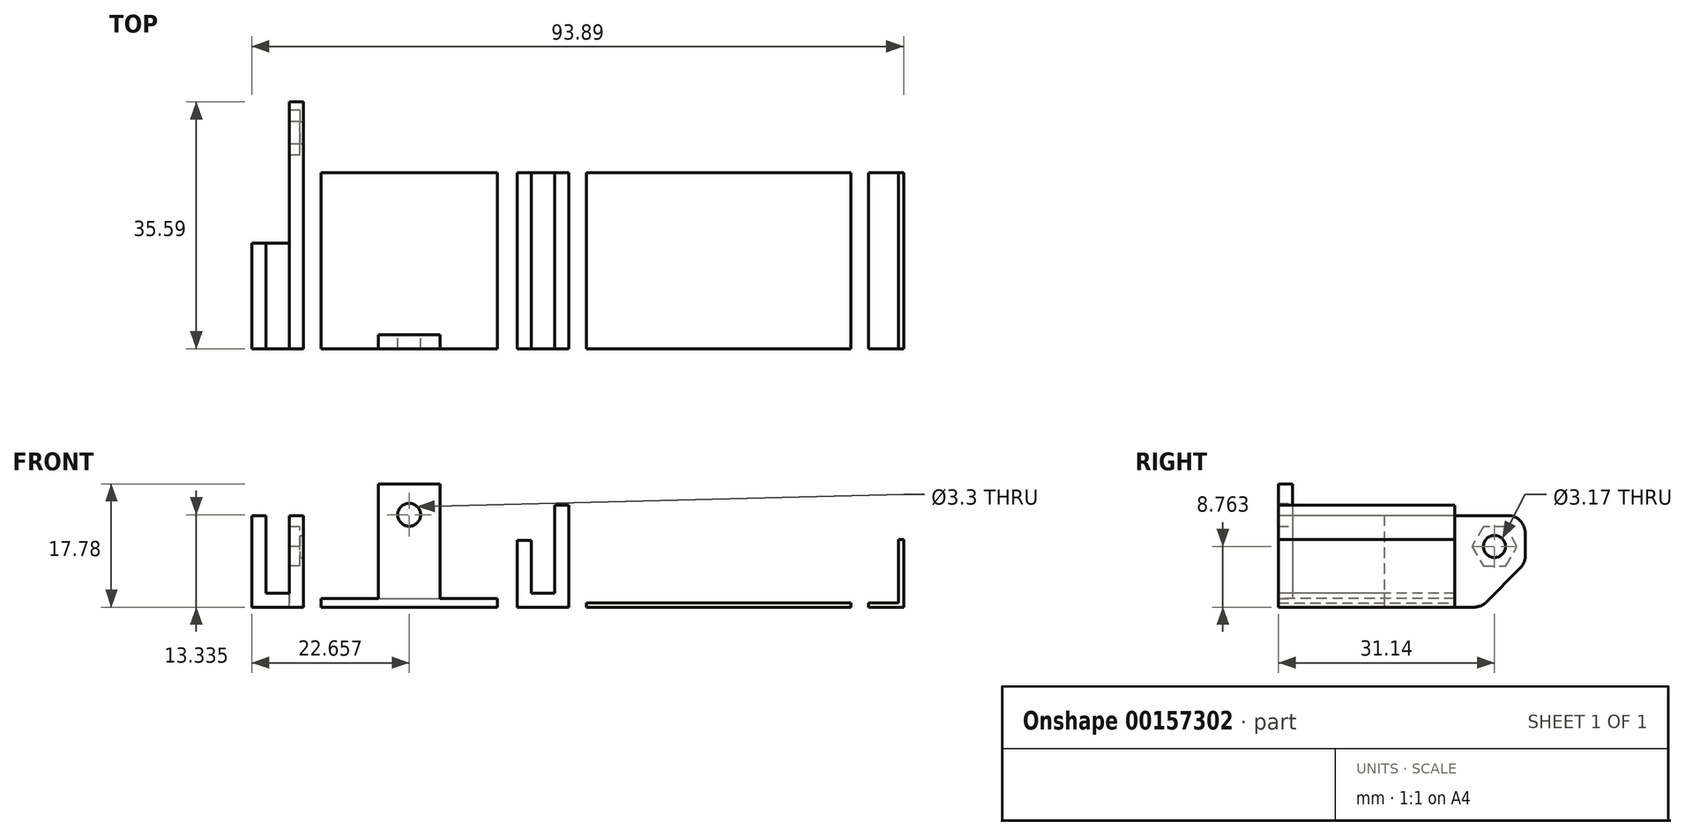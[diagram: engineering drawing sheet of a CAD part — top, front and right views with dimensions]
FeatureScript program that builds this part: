
annotation { "Feature Type Name" : "Feature", "Feature Type Description" : "" }
export const myFeature = defineFeature(function(context is Context, id is Id, definition is map)
    precondition{}
    {
        {
            var Q0;
            Q0=qCreatedBy(makeId("Top.planeOp"),FACE);
            var sketch = newSketch(context, id + "F0", { "sketchPlane" : qUnion([Q0])});
            skLineSegment(sketch, "E0.bottom", {"start": v(2.54, 17.78) * mm, "end": v(9.96, 17.78) * mm});
            skLineSegment(sketch, "E0.top", {"start": v(2.54, 2.54) * mm, "end": v(9.96, 2.54) * mm});
            skLineSegment(sketch, "E0.left", {"start": v(2.54, 17.78) * mm, "end": v(2.54, 2.54) * mm});
            skLineSegment(sketch, "E0.right", {"start": v(9.96, 17.78) * mm, "end": v(9.96, 2.54) * mm});
            skSolve(sketch);
        }
        {
            var Q0;
            Q0 = qSketchRegion(id + "F0", true);
            extrude(context, id + "F1", {"entities" : qUnion([Q0]), "depth" : 2.03 * mm});
        }
        {
            var Q0;
            Q0=makeQuery(id+"F1.opExtrude","CAP_FACE",FACE,{"disambiguationData":[OSD([sQuery(id+"F0.wireOp",EDGE,"E0.bottom"),sQuery(id+"F0.wireOp",EDGE,"E0.top"),sQuery(id+"F0.wireOp",EDGE,"E0.left"),sQuery(id+"F0.wireOp",EDGE,"E0.right")])],"isStart":false});
            var sketch = newSketch(context, id + "F2", { "sketchPlane" : qUnion([Q0])});
            skLineSegment(sketch, "E1.bottom", {"start": v(2.54, 17.78) * mm, "end": v(4.57, 17.78) * mm});
            skLineSegment(sketch, "E1.top", {"start": v(2.54, 2.54) * mm, "end": v(4.57, 2.54) * mm});
            skLineSegment(sketch, "E1.left", {"start": v(2.54, 17.78) * mm, "end": v(2.54, 2.54) * mm});
            skLineSegment(sketch, "E1.right", {"start": v(4.57, 17.78) * mm, "end": v(4.57, 2.54) * mm});
            skLineSegment(sketch, "E2.bottom", {"start": v(9.96, 17.78) * mm, "end": v(7.92, 17.78) * mm});
            skLineSegment(sketch, "E2.top", {"start": v(9.96, 2.54) * mm, "end": v(7.92, 2.54) * mm});
            skLineSegment(sketch, "E2.left", {"start": v(9.96, 17.78) * mm, "end": v(9.96, 2.54) * mm});
            skLineSegment(sketch, "E2.right", {"start": v(7.92, 17.78) * mm, "end": v(7.92, 2.54) * mm});
            skSolve(sketch);
        }
        {
            var Q0;
            Q0 = qSketchRegion(id + "F2", true);
            extrude(context, id + "F3", {"entities" : qUnion([Q0]), "operationType" : NewBodyOperationType.ADD, "depth" : 11.18 * mm});
        }
        {
            var Q0;
            Q0=makeQuery(id+"F3.boolean.opBoolean","MERGE",FACE,{"derivedFrom":[makeQuery(id+"F1.opExtrude","SWEPT_FACE",FACE,{"disambiguationData":[OSD([sQuery(id+"F0.wireOp",EDGE,"E0.right")])]}),makeQuery(id+"F3.opExtrude","SWEPT_FACE",FACE,{"disambiguationData":[OSD([sQuery(id+"F2.wireOp",EDGE,"E2.left")])]})]});
            var sketch = newSketch(context, id + "F4", { "sketchPlane" : qUnion([Q0])});
            skLineSegment(sketch, "E3.bottom", {"start": v(17.78, 0) * mm, "end": v(30.72, 0) * mm});
            skLineSegment(sketch, "E3.top", {"start": v(17.78, 13.2) * mm, "end": v(35.59, 13.2) * mm});
            skLineSegment(sketch, "E3.left", {"start": v(17.78, 0) * mm, "end": v(17.78, 13.2) * mm});
            skLineSegment(sketch, "E3.right", {"start": v(38.13, 7.4) * mm, "end": v(38.13, 10.67) * mm});
            skCircle(sketch, "E4", {"center": v(33.68, 8.76) * mm, "radius": 1.59 * mm});
            skLineSegment(sketch, "E5", {"start": v(32.52, 0.74) * mm, "end": v(37.38, 5.6) * mm});
            skPoint(sketch, "E6.visualSharp", {"position": v(31.78, 0) * mm});
            skArc(sketch, "E6.filletArc", {"start": v(30.72, 0) * mm, "mid": v(31.7, 0.2) * mm, "end": v(32.52, 0.74) * mm});
            skPoint(sketch, "E7.visualSharp", {"position": v(38.13, 6.35) * mm});
            skArc(sketch, "E7.filletArc", {"start": v(37.38, 5.6) * mm, "mid": v(37.93, 6.43) * mm, "end": v(38.13, 7.4) * mm});
            skPoint(sketch, "E8.visualSharp", {"position": v(38.13, 13.2) * mm});
            skArc(sketch, "E8.filletArc", {"start": v(38.13, 10.67) * mm, "mid": v(37.38, 12.46) * mm, "end": v(35.59, 13.2) * mm});
            skSolve(sketch);
        }
        {
            var Q0;
            Q0 = qSketchRegion(id + "F4", true);
            extrude(context, id + "F5", {"entities" : qUnion([Q0]), "operationType" : NewBodyOperationType.ADD, "oppositeDirection" : true, "depth" : 2.03 * mm});
        }
        {
            var Q0;
            Q0=makeQuery(id+"F5.opExtrude","CAP_FACE",FACE,{"disambiguationData":[OSD([sQuery(id+"F4.wireOp",EDGE,"E3.bottom"),sQuery(id+"F4.wireOp",EDGE,"E3.top"),sQuery(id+"F4.wireOp",EDGE,"E3.left"),sQuery(id+"F4.wireOp",EDGE,"E3.right")])],"isStart":false});
            var sketch = newSketch(context, id + "F6", { "sketchPlane" : qUnion([Q0])});
            skCircle(sketch, "E9.cCircle", {"center": v(-33.68, 8.76) * mm, "radius": 2.82 * mm, "construction": true});
            skLineSegment(sketch, "E9.0", {"start": v(-36.94, 8.76) * mm, "end": v(-35.3, 11.58) * mm});
            skLineSegment(sketch, "E9.1", {"start": v(-35.3, 11.58) * mm, "end": v(-32.05, 11.58) * mm});
            skLineSegment(sketch, "E9.2", {"start": v(-32.05, 11.58) * mm, "end": v(-30.42, 8.76) * mm});
            skLineSegment(sketch, "E9.3", {"start": v(-30.42, 8.76) * mm, "end": v(-32.05, 5.94) * mm});
            skLineSegment(sketch, "E9.4", {"start": v(-32.05, 5.94) * mm, "end": v(-35.3, 5.94) * mm});
            skLineSegment(sketch, "E9.5", {"start": v(-35.3, 5.94) * mm, "end": v(-36.94, 8.76) * mm});
            skPoint(sketch, "E9.0.midPoint", {"position": v(-36.12, 10.17) * mm});
            skSolve(sketch);
        }
        {
            var Q0;
            Q0 = qSketchRegion(id + "F6", true);
            extrude(context, id + "F7", {"entities" : qUnion([Q0]), "operationType" : NewBodyOperationType.REMOVE, "oppositeDirection" : true, "depth" : 1.52 * mm});
        }
        {
            var Q0;
            Q0=qCreatedBy(makeId("Top.planeOp"),FACE);
            var sketch = newSketch(context, id + "F8", { "sketchPlane" : qUnion([Q0])});
            skLineSegment(sketch, "E10.bottom", {"start": v(12.5, 27.94) * mm, "end": v(37.9, 27.94) * mm});
            skLineSegment(sketch, "E10.top", {"start": v(12.5, 2.54) * mm, "end": v(37.9, 2.54) * mm});
            skLineSegment(sketch, "E10.left", {"start": v(12.5, 27.94) * mm, "end": v(12.5, 2.54) * mm});
            skLineSegment(sketch, "E10.right", {"start": v(37.9, 27.94) * mm, "end": v(37.9, 2.54) * mm});
            skSolve(sketch);
        }
        {
            var Q0;
            Q0 = qSketchRegion(id + "F8", true);
            extrude(context, id + "F9", {"entities" : qUnion([Q0]), "depth" : 1.27 * mm});
        }
        {
            var Q0;
            Q0=makeQuery(id+"F9.opExtrude","CAP_FACE",FACE,{"disambiguationData":[OSD([sQuery(id+"F8.wireOp",EDGE,"E10.bottom"),sQuery(id+"F8.wireOp",EDGE,"E10.top"),sQuery(id+"F8.wireOp",EDGE,"E10.left"),sQuery(id+"F8.wireOp",EDGE,"E10.right")])],"isStart":false});
            var sketch = newSketch(context, id + "F10", { "sketchPlane" : qUnion([Q0])});
            skLineSegment(sketch, "E11.bottom", {"start": v(20.75, 2.54) * mm, "end": v(29.64, 2.54) * mm});
            skLineSegment(sketch, "E11.top", {"start": v(20.75, 4.57) * mm, "end": v(29.64, 4.57) * mm});
            skLineSegment(sketch, "E11.left", {"start": v(20.75, 2.54) * mm, "end": v(20.75, 4.57) * mm});
            skLineSegment(sketch, "E11.right", {"start": v(29.64, 2.54) * mm, "end": v(29.64, 4.57) * mm});
            skSolve(sketch);
        }
        {
            var Q0;
            Q0 = qSketchRegion(id + "F10", true);
            extrude(context, id + "F11", {"entities" : qUnion([Q0]), "operationType" : NewBodyOperationType.ADD, "depth" : 16.5 * mm});
        }
        {
            var Q0;
            Q0=makeQuery(id+"F11.opExtrude","SWEPT_FACE",FACE,{"disambiguationData":[OSD([sQuery(id+"F10.wireOp",EDGE,"E11.top")])]});
            var sketch = newSketch(context, id + "F12", { "sketchPlane" : qUnion([Q0])});
            skCircle(sketch, "E12", {"center": v(-25.2, 13.34) * mm, "radius": 1.65 * mm});
            skSolve(sketch);
        }
        {
            var Q0;
            Q0 = qSketchRegion(id + "F12", true);
            extrude(context, id + "F13", {"entities" : qUnion([Q0]), "operationType" : NewBodyOperationType.REMOVE, "endBound" : BoundingType.UP_TO_NEXT, "oppositeDirection" : true, "depth" : 25.4 * mm});
        }
        {
            var Q0;
            Q0=qCreatedBy(makeId("Top.planeOp"),FACE);
            var sketch = newSketch(context, id + "F14", { "sketchPlane" : qUnion([Q0])});
            skLineSegment(sketch, "E13.bottom", {"start": v(40.75, 27.94) * mm, "end": v(48.17, 27.94) * mm});
            skLineSegment(sketch, "E13.top", {"start": v(40.75, 2.54) * mm, "end": v(48.17, 2.54) * mm});
            skLineSegment(sketch, "E13.left", {"start": v(40.75, 27.94) * mm, "end": v(40.75, 2.54) * mm});
            skLineSegment(sketch, "E13.right", {"start": v(48.17, 27.94) * mm, "end": v(48.17, 2.54) * mm});
            skSolve(sketch);
        }
        {
            var Q0;
            Q0 = qSketchRegion(id + "F14", true);
            extrude(context, id + "F15", {"entities" : qUnion([Q0]), "depth" : 2.03 * mm});
        }
        {
            var Q0;
            Q0=makeQuery(id+"F15.opExtrude","CAP_FACE",FACE,{"disambiguationData":[OSD([sQuery(id+"F14.wireOp",EDGE,"E13.bottom"),sQuery(id+"F14.wireOp",EDGE,"E13.top"),sQuery(id+"F14.wireOp",EDGE,"E13.left"),sQuery(id+"F14.wireOp",EDGE,"E13.right")])],"isStart":false});
            var sketch = newSketch(context, id + "F16", { "sketchPlane" : qUnion([Q0])});
            skLineSegment(sketch, "E14.bottom", {"start": v(40.75, 27.94) * mm, "end": v(42.78, 27.94) * mm});
            skLineSegment(sketch, "E14.top", {"start": v(40.75, 2.54) * mm, "end": v(42.78, 2.54) * mm});
            skLineSegment(sketch, "E14.left", {"start": v(40.75, 27.94) * mm, "end": v(40.75, 2.54) * mm});
            skLineSegment(sketch, "E14.right", {"start": v(42.78, 27.94) * mm, "end": v(42.78, 2.54) * mm});
            skLineSegment(sketch, "E15.bottom", {"start": v(48.17, 27.94) * mm, "end": v(46.13, 27.94) * mm});
            skLineSegment(sketch, "E15.top", {"start": v(48.17, 2.54) * mm, "end": v(46.13, 2.54) * mm});
            skLineSegment(sketch, "E15.left", {"start": v(48.17, 27.94) * mm, "end": v(48.17, 2.54) * mm});
            skLineSegment(sketch, "E15.right", {"start": v(46.13, 27.94) * mm, "end": v(46.13, 2.54) * mm});
            skSolve(sketch);
        }
        {
            var Q0;
            Q0 = qSketchRegion(id + "F16", true);
            extrude(context, id + "F17", {"entities" : qUnion([Q0]), "operationType" : NewBodyOperationType.ADD, "depth" : 12.7 * mm});
        }
        {
            var Q0;
            Q0=makeQuery(id+"F17.boolean.opBoolean","MERGE",FACE,{"derivedFrom":[makeQuery(id+"F15.opExtrude","SWEPT_FACE",FACE,{"disambiguationData":[OSD([sQuery(id+"F14.wireOp",EDGE,"E13.top")])]}),makeQuery(id+"F17.opExtrude","SWEPT_FACE",FACE,{"disambiguationData":[OSD([sQuery(id+"F16.wireOp",EDGE,"E14.top")])]}),makeQuery(id+"F17.opExtrude","SWEPT_FACE",FACE,{"disambiguationData":[OSD([sQuery(id+"F16.wireOp",EDGE,"E15.top")])]})]});
            var sketch = newSketch(context, id + "F18", { "sketchPlane" : qUnion([Q0])});
            skLineSegment(sketch, "E16.bottom", {"start": v(40.75, 14.73) * mm, "end": v(42.78, 14.73) * mm});
            skLineSegment(sketch, "E16.top", {"start": v(40.75, 9.65) * mm, "end": v(42.78, 9.65) * mm});
            skLineSegment(sketch, "E16.left", {"start": v(40.75, 14.73) * mm, "end": v(40.75, 9.65) * mm});
            skLineSegment(sketch, "E16.right", {"start": v(42.78, 14.73) * mm, "end": v(42.78, 9.65) * mm});
            skSolve(sketch);
        }
        {
            var Q0;
            Q0 = qSketchRegion(id + "F18", true);
            extrude(context, id + "F19", {"entities" : qUnion([Q0]), "operationType" : NewBodyOperationType.REMOVE, "endBound" : BoundingType.UP_TO_NEXT, "oppositeDirection" : true, "depth" : 25.4 * mm});
        }
        {
            var Q0;
            Q0=qCreatedBy(makeId("Top.planeOp"),FACE);
            var sketch = newSketch(context, id + "F20", { "sketchPlane" : qUnion([Q0])});
            skLineSegment(sketch, "E17.bottom", {"start": v(50.7, 2.54) * mm, "end": v(88.8, 2.54) * mm});
            skLineSegment(sketch, "E17.top", {"start": v(50.7, 27.94) * mm, "end": v(88.8, 27.94) * mm});
            skLineSegment(sketch, "E17.left", {"start": v(50.7, 2.54) * mm, "end": v(50.7, 27.94) * mm});
            skLineSegment(sketch, "E17.right", {"start": v(88.8, 2.54) * mm, "end": v(88.8, 27.94) * mm});
            skLineSegment(sketch, "E18.bottom", {"start": v(91.35, 27.94) * mm, "end": v(96.43, 27.94) * mm});
            skLineSegment(sketch, "E18.top", {"start": v(91.35, 2.54) * mm, "end": v(96.43, 2.54) * mm});
            skLineSegment(sketch, "E18.left", {"start": v(91.35, 27.94) * mm, "end": v(91.35, 2.54) * mm});
            skLineSegment(sketch, "E18.right", {"start": v(96.43, 27.94) * mm, "end": v(96.43, 2.54) * mm});
            skSolve(sketch);
        }
        {
            var Q0;
            Q0 = qSketchRegion(id + "F20", true);
            extrude(context, id + "F21", {"entities" : qUnion([Q0]), "depth" : 0.64 * mm});
        }
        {
            var Q0;
            Q0=makeQuery(id+"F21.opExtrude","CAP_FACE",FACE,{"disambiguationData":[OSD([sQuery(id+"F20.wireOp",EDGE,"E18.bottom"),sQuery(id+"F20.wireOp",EDGE,"E18.top"),sQuery(id+"F20.wireOp",EDGE,"E18.left"),sQuery(id+"F20.wireOp",EDGE,"E18.right")])],"isStart":false});
            var sketch = newSketch(context, id + "F22", { "sketchPlane" : qUnion([Q0])});
            skLineSegment(sketch, "E19.bottom", {"start": v(96.43, 27.94) * mm, "end": v(95.66, 27.94) * mm});
            skLineSegment(sketch, "E19.top", {"start": v(96.43, 2.54) * mm, "end": v(95.66, 2.54) * mm});
            skLineSegment(sketch, "E19.left", {"start": v(96.43, 27.94) * mm, "end": v(96.43, 2.54) * mm});
            skLineSegment(sketch, "E19.right", {"start": v(95.66, 27.94) * mm, "end": v(95.66, 2.54) * mm});
            skSolve(sketch);
        }
        {
            var Q0;
            Q0 = qSketchRegion(id + "F22", true);
            extrude(context, id + "F23", {"entities" : qUnion([Q0]), "operationType" : NewBodyOperationType.ADD, "depth" : 9.14 * mm});
        }
    });
